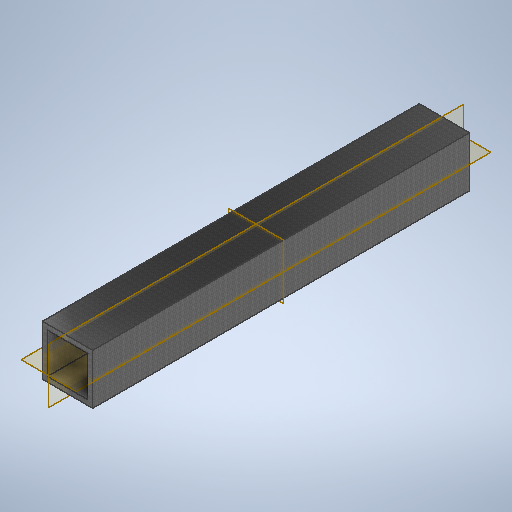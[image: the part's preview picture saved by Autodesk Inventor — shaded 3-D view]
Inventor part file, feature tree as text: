
AUTODESK INVENTOR PART (.ipt)
format: ipt  version: 2025.2 (Build 292293000, 293)  size: 297,984 bytes
history: native  units: mm
features: extrude x1, sketch x1
ambient origin geometry x8: Origin, YZ Plane, XZ Plane, XY Plane, X Axis, Y Axis, Z Axis, Center Point
bodies: Solid1 (feature_tree)
feature tree (2):
  extrude  "Extrusion1"  Depth=100.0mm
  sketch  "Sketch1"  dims[d0=100.0mm d1=100.0mm d2=10.0mm d3=750.0mm d4=0.0mm d5=0.5mm d6=0.872665mm]
